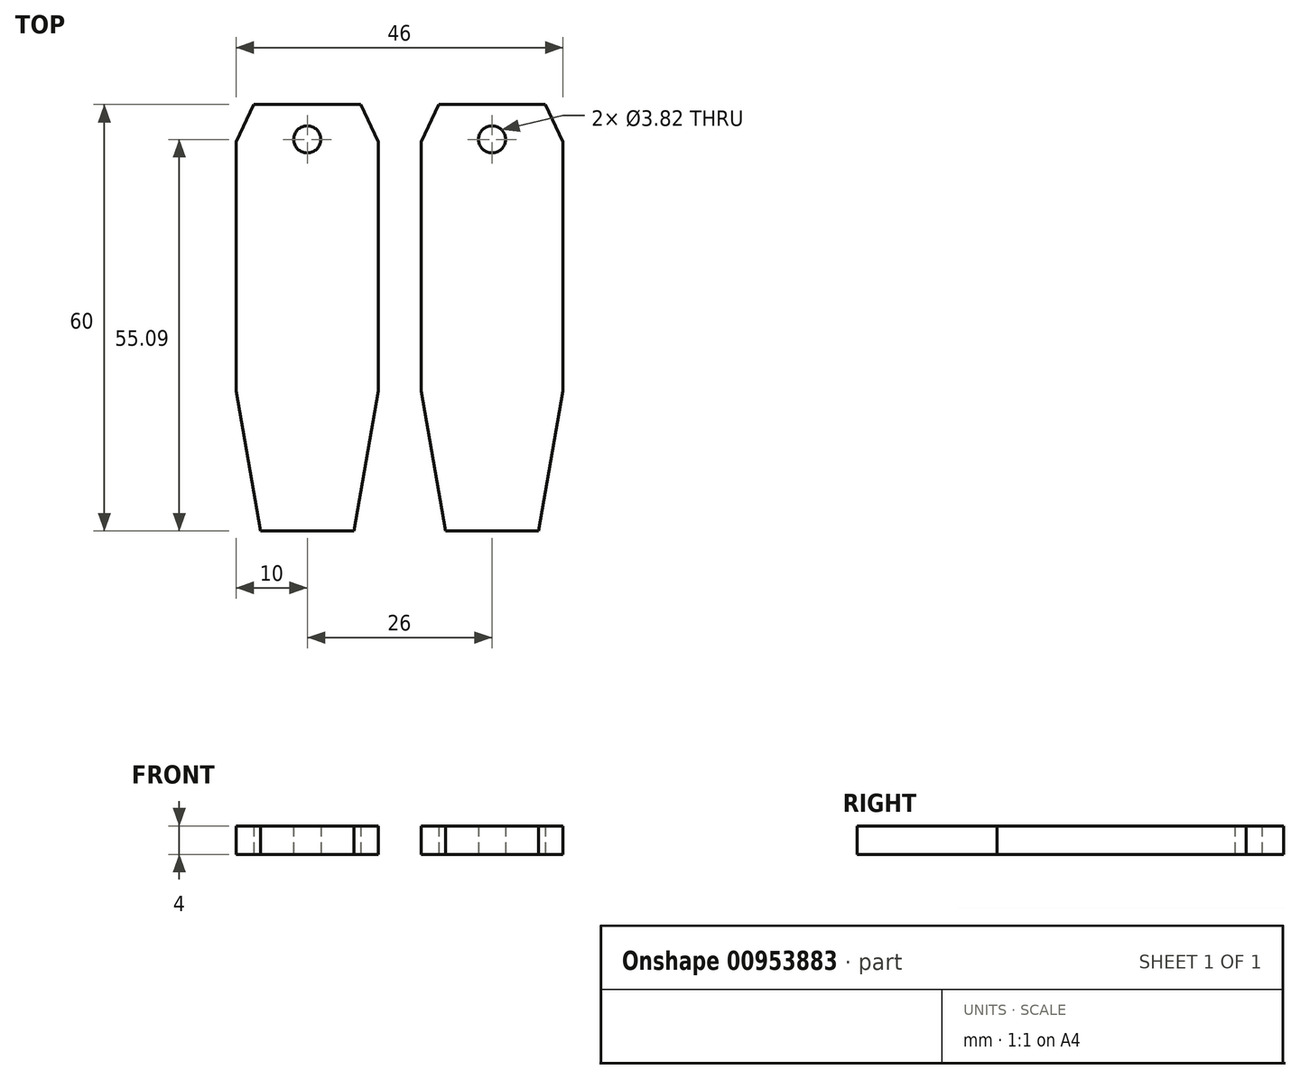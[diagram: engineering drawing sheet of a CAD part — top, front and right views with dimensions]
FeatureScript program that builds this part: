
annotation { "Feature Type Name" : "Feature", "Feature Type Description" : "" }
export const myFeature = defineFeature(function(context is Context, id is Id, definition is map)
    precondition{}
    {
        {
            var Q0;
            Q0=qCreatedBy(makeId("Top.planeOp"),FACE);
            var sketch = newSketch(context, id + "F0", { "sketchPlane" : qUnion([Q0])});
            skLineSegment(sketch, "E0.bottom", {"start": v(6.55, -30) * mm, "end": v(-6.55, -30) * mm});
            skLineSegment(sketch, "E0.top", {"start": v(7.5, 30) * mm, "end": v(-7.5, 30) * mm});
            skLineSegment(sketch, "E0.left", {"start": v(10, -10.3) * mm, "end": v(10, 24.72) * mm});
            skLineSegment(sketch, "E0.right", {"start": v(-10, -10.3) * mm, "end": v(-10, 24.72) * mm});
            skPoint(sketch, "E0.middle", {"position": v(0, 0) * mm});
            skLineSegment(sketch, "E1", {"start": v(0, 30) * mm, "end": v(0, 35.95) * mm, "construction": true});
            skLineSegment(sketch, "E2", {"start": v(0, 35.95) * mm, "end": v(-10, 35.95) * mm, "construction": true});
            skLineSegment(sketch, "E3", {"start": v(0, 35.95) * mm, "end": v(10, 35.95) * mm, "construction": true});
            skLineSegment(sketch, "E4", {"start": v(-10, 35.95) * mm, "end": v(-7.5, 35.95) * mm});
            skLineSegment(sketch, "E5", {"start": v(10, 35.95) * mm, "end": v(7.5, 35.95) * mm, "construction": true});
            skLineSegment(sketch, "E6", {"start": v(-7.5, 30) * mm, "end": v(-10, 24.72) * mm});
            skLineSegment(sketch, "E7", {"start": v(0, 30) * mm, "end": v(0, -30) * mm, "construction": true});
            skLineSegment(sketch, "E8.MirrorCS", {"start": v(7.5, 30) * mm, "end": v(10, 24.72) * mm});
            skPoint(sketch, "E9.orphan", {"position": v(-10, 30) * mm});
            skPoint(sketch, "E10.orphan", {"position": v(10, 30) * mm});
            skLineSegment(sketch, "E11", {"start": v(-6.55, -30) * mm, "end": v(-10, -10.3) * mm});
            skLineSegment(sketch, "E12.MirrorCS", {"start": v(6.55, -30) * mm, "end": v(10, -10.3) * mm});
            skPoint(sketch, "E13.orphan", {"position": v(-10, -30) * mm});
            skPoint(sketch, "E14.orphan", {"position": v(10, -30) * mm});
            skCircle(sketch, "E15", {"center": v(0, 25.09) * mm, "radius": 1.91 * mm});
            skSolve(sketch);
        }
        {
            var Q0;
            Q0 = qSketchRegion(id + "F0", true);
            extrude(context, id + "F1", {"entities" : qUnion([Q0]), "depth" : 4 * mm, "offsetDistance" : 25 * mm});
        }
        {
            var Q0;
            Q0=qCreatedBy(makeId("Right.planeOp"),FACE);
            cPlane(context, id + "F2", {"entities" : qUnion([Q0]), "cplaneType" : CPlaneType.OFFSET, "offset" : 13 * mm, "width" : 150 * mm, "height" : 150 * mm});
        }
        {
            var Q0;
            Q0=makeQuery(id+"F1.opExtrude","SWEPT_BODY",BODY,{"disambiguationData":[OSD([sQuery(id+"F0.wireOp",EDGE,"E0.bottom"),sQuery(id+"F0.wireOp",EDGE,"E0.top"),sQuery(id+"F0.wireOp",EDGE,"E0.left"),sQuery(id+"F0.wireOp",EDGE,"E0.right"),sQuery(id+"F0.wireOp",EDGE,"E6"),sQuery(id+"F0.wireOp",EDGE,"E8.MirrorCS"),sQuery(id+"F0.wireOp",EDGE,"E11"),sQuery(id+"F0.wireOp",EDGE,"E12.MirrorCS"),sQuery(id+"F0.wireOp",EDGE,"E15")])]});
            var Q1;
            Q1=qCreatedBy(id+"F2.planeOp",FACE);
            mirror(context, id + "F3", {"entities" : qUnion([Q0]), "mirrorPlane" : qUnion([Q1])});
        }
    });
